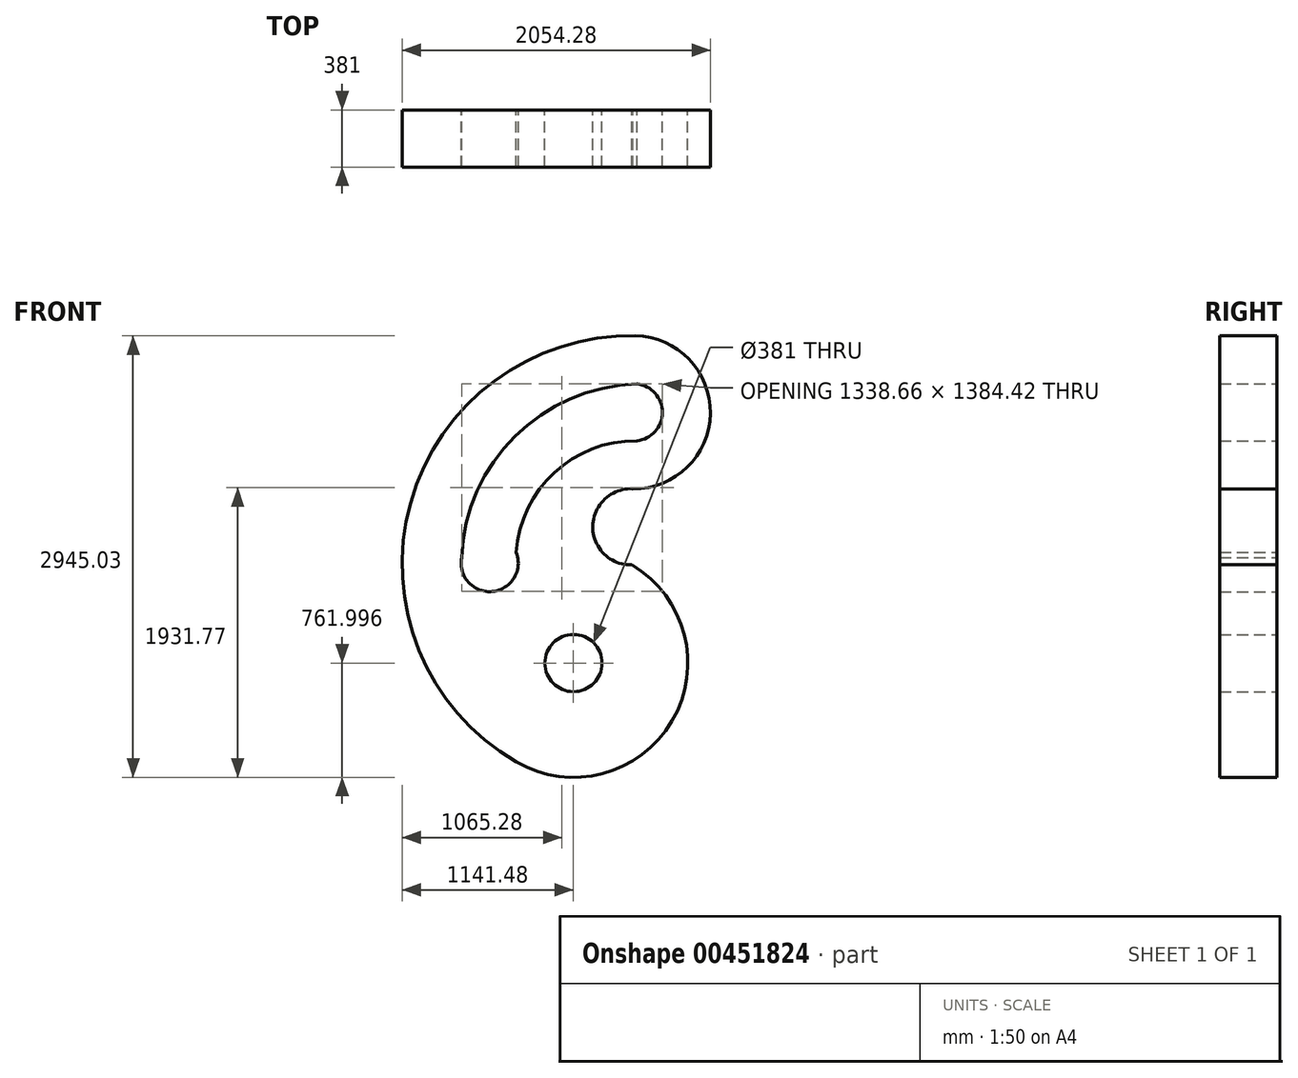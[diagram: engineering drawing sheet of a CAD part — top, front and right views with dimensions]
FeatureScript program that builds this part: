
annotation { "Feature Type Name" : "Feature", "Feature Type Description" : "" }
export const myFeature = defineFeature(function(context is Context, id is Id, definition is map)
    precondition{}
    {
        {
            var Q0;
            Q0=qCreatedBy(makeId("Front.planeOp"),FACE);
            var sketch = newSketch(context, id + "F0", { "sketchPlane" : qUnion([Q0])});
            skArc(sketch, "E0", {"start": v(30.22, 1523.7) * mm, "mid": v(-1467.62, 410.7) * mm, "end": v(-765.03, -1318.07) * mm});
            skArc(sketch, "E1", {"start": v(-1128.05, 44.28) * mm, "mid": v(-922.6, -181.47) * mm, "end": v(-764.42, 79.59) * mm});
            skArc(sketch, "E2", {"start": v(40.03, 824.17) * mm, "mid": v(210.6, 1013.05) * mm, "end": v(41.16, 1202.95) * mm});
            skArc(sketch, "E3", {"start": v(14.16, 503.48) * mm, "mid": v(530.22, 1005.6) * mm, "end": v(30.22, 1523.7) * mm});
            skCircle(sketch, "E4", {"center": v(-382.52, -659.03) * mm, "radius": 190.5 * mm});
            skArc(sketch, "E5", {"start": v(-765.03, -1318.07) * mm, "mid": v(276.52, -1041.55) * mm, "end": v(0, 0) * mm});
            skArc(sketch, "E6.0", {"start": v(41.16, 1202.95) * mm, "mid": v(-771.7, 853.95) * mm, "end": v(-1128.05, 44.28) * mm});
            skArc(sketch, "E7.0", {"start": v(40.03, 824.17) * mm, "mid": v(-509.75, 611.3) * mm, "end": v(-764.42, 79.59) * mm});
            skPoint(sketch, "E8.trimOffspring.end.orphan", {"position": v(0, 1578.63) * mm});
            skLineSegment(sketch, "E9", {"start": v(14.16, 503.41) * mm, "end": v(14.16, 503.48) * mm});
            skLineSegment(sketch, "E10", {"start": v(6.97, -4.1) * mm, "end": v(-13.52, -3.83) * mm});
            skArc(sketch, "E11", {"start": v(14.16, 503.41) * mm, "mid": v(-253.97, 253.4) * mm, "end": v(6.97, -4.1) * mm});
            skSolve(sketch);
        }
        {
            var Q0;
            {var subQ5=sQuery(id+"F0.wireOp",EDGE,"E0");Q0=makeQuery(id+"F0.imprint","IMPRINT",FACE,{"disambiguationData":[TD([[makeQuery(id+"F0.imprint","IMPRINT",EDGE,{"derivedFrom":subQ5}),1.0]])]});}
            extrude(context, id + "F1", {"entities" : qUnion([Q0]), "depth" : 381 * mm});
        }
    });
